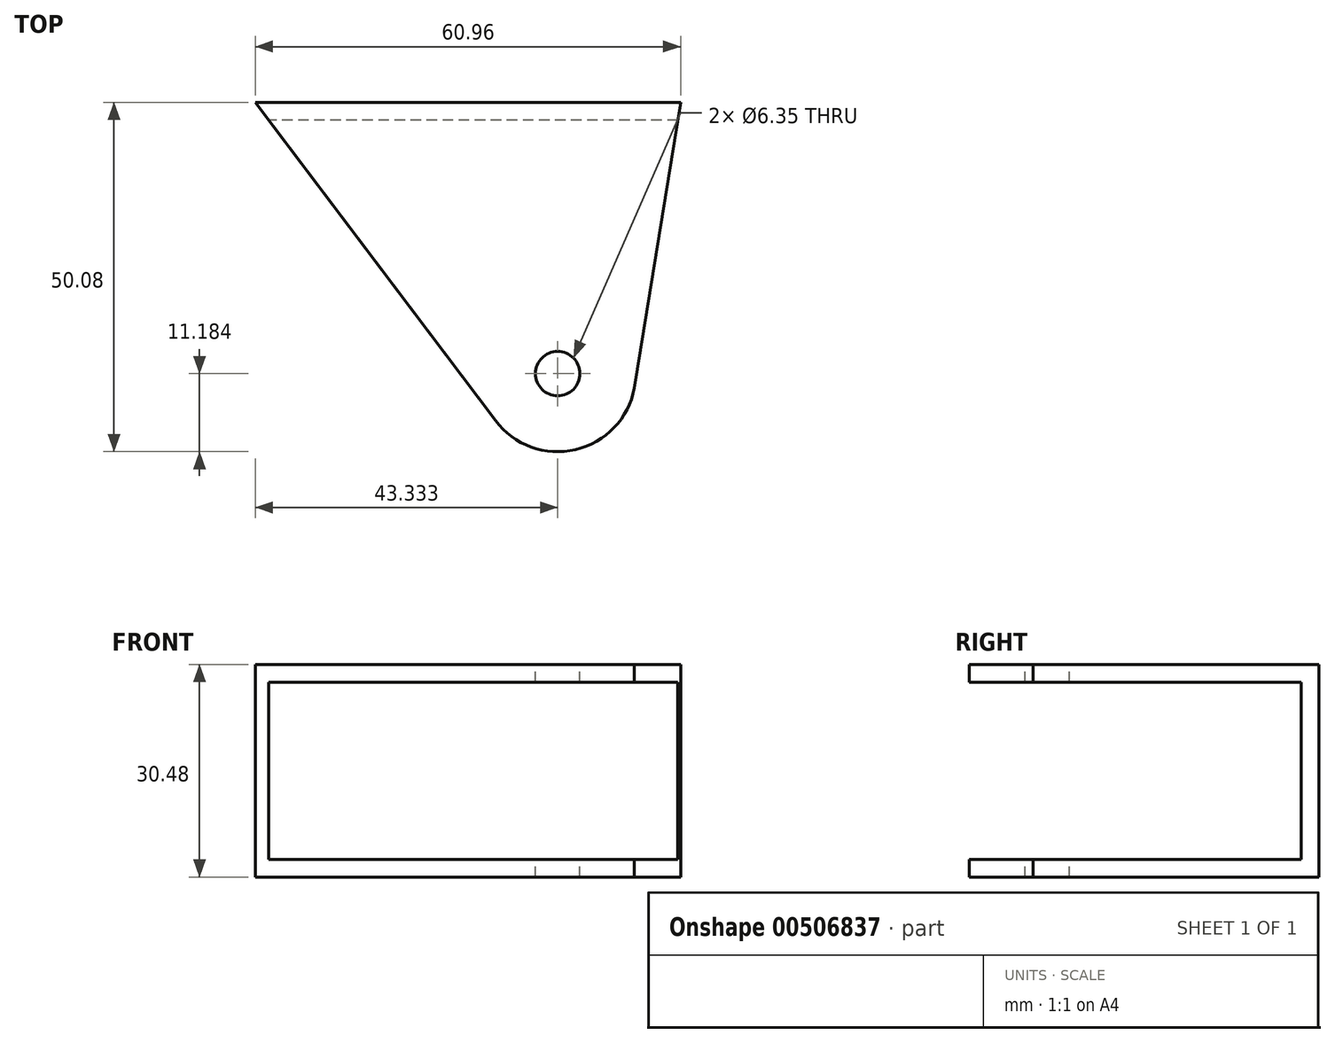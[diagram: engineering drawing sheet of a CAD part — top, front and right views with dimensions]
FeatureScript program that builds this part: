
annotation { "Feature Type Name" : "Feature", "Feature Type Description" : "" }
export const myFeature = defineFeature(function(context is Context, id is Id, definition is map)
    precondition{}
    {
        {
            var Q0;
            Q0=qCreatedBy(makeId("Top.planeOp"),FACE);
            var sketch = newSketch(context, id + "F0", { "sketchPlane" : qUnion([Q0])});
            skLineSegment(sketch, "E0", {"start": v(35.06, 45.63) * mm, "end": v(-25.9, 45.63) * mm});
            skLineSegment(sketch, "E1", {"start": v(-25.9, 45.63) * mm, "end": v(8.5, 0) * mm});
            skLineSegment(sketch, "E2", {"start": v(35.06, 45.63) * mm, "end": v(28.42, 4.66) * mm});
            skArc(sketch, "E3", {"start": v(8.5, 0) * mm, "mid": v(19.98, -4.16) * mm, "end": v(28.42, 4.66) * mm});
            skSolve(sketch);
        }
        {
            var Q0;
            Q0=makeQuery(id+"F0.imprint","IMPRINT",FACE,{"disambiguationData":[TD([[makeQuery(id+"F0.imprint","IMPRINT",EDGE,{"derivedFrom":sQuery(id+"F0.wireOp",EDGE,"E0")}),1.0]])]});
            extrude(context, id + "F1", {"entities" : qUnion([Q0]), "depth" : 30.48 * mm, "offsetDistance" : 25.4 * mm});
        }
        {
            var Q0;
            Q0=makeQuery(id+"F1.opExtrude","SWEPT_FACE",FACE,{"disambiguationData":[OSD([sQuery(id+"F0.wireOp",EDGE,"E3")])]});
            var Q1;
            Q1=makeQuery(id+"F1.opExtrude","SWEPT_FACE",FACE,{"disambiguationData":[OSD([sQuery(id+"F0.wireOp",EDGE,"E2")])]});
            var Q2;
            Q2=makeQuery(id+"F1.opExtrude","SWEPT_FACE",FACE,{"disambiguationData":[OSD([sQuery(id+"F0.wireOp",EDGE,"E1")])]});
            shell(context, id + "F2", {"entities" : qUnion([Q0, Q1, Q2]), "thickness" : 2.54 * mm});
        }
        {
            var Q0;
            Q0=makeQuery(id+"F1.opExtrude","CAP_FACE",FACE,{"disambiguationData":[OSD([sQuery(id+"F0.wireOp",EDGE,"E0"),sQuery(id+"F0.wireOp",EDGE,"E1"),sQuery(id+"F0.wireOp",EDGE,"E2"),sQuery(id+"F0.wireOp",EDGE,"E3")])],"isStart":false});
            var sketch = newSketch(context, id + "F3", { "sketchPlane" : qUnion([Q0])});
            skPoint(sketch, "E4", {"position": v(17.43, 6.73) * mm});
            skSolve(sketch);
        }
        {
            var Q0;
            Q0=sQuery(id+"F3.wireOp",VERTEX,"E4");
            var Q1;
            Q1=makeQuery(id+"F1.opExtrude","SWEPT_BODY",BODY,{"disambiguationData":[OSD([sQuery(id+"F0.wireOp",EDGE,"E0"),sQuery(id+"F0.wireOp",EDGE,"E1"),sQuery(id+"F0.wireOp",EDGE,"E2"),sQuery(id+"F0.wireOp",EDGE,"E3")])]});
            hole(context, id + "F4", {"style" : HoleStyle.SIMPLE, "endStyle" : HoleEndStyle.THROUGH, "holeDiameter" : 6.35 * mm, "majorDiameter" : 6.35 * mm, "isTappedThrough" : true, "tappedDepth" : 12.7 * mm, "tapClearance" : 3, "locations" : qUnion([Q0]), "scope" : qUnion([Q1])});
        }
    });
